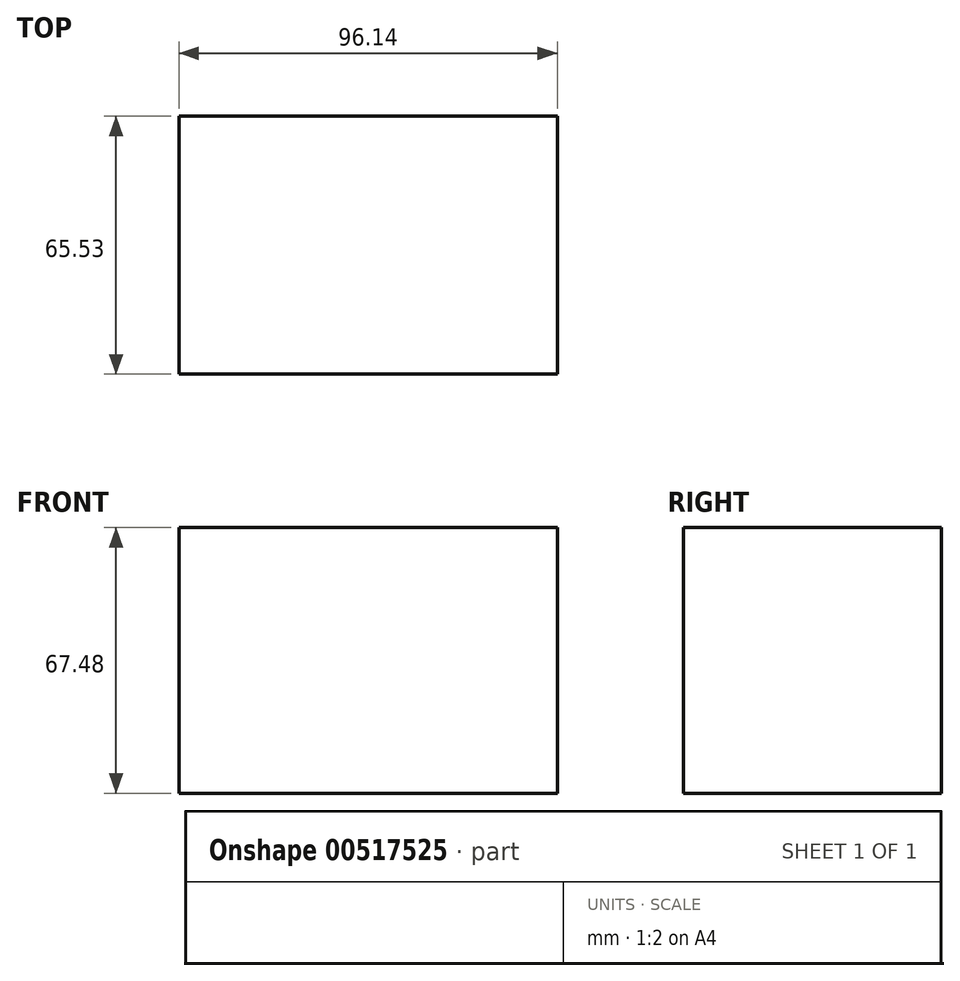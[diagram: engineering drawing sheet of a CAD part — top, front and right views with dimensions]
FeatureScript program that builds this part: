
annotation { "Feature Type Name" : "Feature", "Feature Type Description" : "" }
export const myFeature = defineFeature(function(context is Context, id is Id, definition is map)
    precondition{}
    {
        {
            var Q0;
            Q0=qCreatedBy(makeId("Top.planeOp"),FACE);
            var sketch = newSketch(context, id + "F0", { "sketchPlane" : qUnion([Q0])});
            skLineSegment(sketch, "E0.bottom", {"start": v(32.67, 0) * mm, "end": v(-63.47, 0) * mm});
            skLineSegment(sketch, "E0.top", {"start": v(32.67, 65.53) * mm, "end": v(-63.47, 65.53) * mm});
            skLineSegment(sketch, "E0.left", {"start": v(32.67, 0) * mm, "end": v(32.67, 65.53) * mm});
            skLineSegment(sketch, "E0.right", {"start": v(-63.47, 0) * mm, "end": v(-63.47, 65.53) * mm});
            skSolve(sketch);
        }
        {
            var Q0;
            Q0=makeQuery(id+"F0.imprint","IMPRINT",FACE,{"disambiguationData":[TD([[makeQuery(id+"F0.imprint","IMPRINT",EDGE,{"derivedFrom":sQuery(id+"F0.wireOp",EDGE,"E0.bottom")}),-1.0]])]});
            extrude(context, id + "F1", {"entities" : qUnion([Q0]), "depth" : 67.48 * mm, "offsetDistance" : 25.4 * mm});
        }
    });
